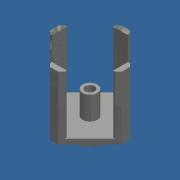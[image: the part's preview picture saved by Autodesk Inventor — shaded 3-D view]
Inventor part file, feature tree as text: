
AUTODESK INVENTOR PART (.ipt)
format: ipt  version: 2020 (Build 240168000, 168)  size: 2,207,232 bytes
history: mixed  units: mm
features: sketch x5, extrude x4, hole x1, pattern_circular x1, chamfer x1, fillet x1, imported_body x1
ambient origin geometry x8: Origin, YZ Plane, XZ Plane, XY Plane, X Axis, Y Axis, Z Axis, Center Point
bodies: Solid1 (imported_parasolid)
feature tree (14):
  extrude  "Extrusion1"  Depth=4.0mm TaperAngle=0.0deg
  extrude  "Extrusion3"  Depth=68.0mm
  extrude  "Extrusion4"  Depth=14.0mm
  extrude  "Extrusion5"  Depth=5.0mm
  hole  "Hole6"  [1 undecoded]
  pattern_circular  "Circular Pattern2"  [2 undecoded]
  chamfer  "Chamfer2"  Distance=14.0mm
  sketch  "Sketch1"  dims[d0=35.0mm d1=4.0mm d2=0.0mm]
  sketch  "Sketch4"  dims[d42=68.0mm d43=68.0mm]
  sketch  "Sketch5"  dims[d44=5.0mm d45=0.0mm d46=14.0mm]
  sketch  "Sketch7"  dims[d47=5.0mm d48=29.0mm]
  sketch  "Sketch8"  dims[d49=7.0mm d50=55.0mm d51=0.0mm d69=4.0mm d70=0.0mm d78=14.0mm d79=22.0mm d80=0.0mm d81=8.5mm d82=6.0mm d83=4.0mm d84=2.0mm d85=90.0deg d86=51.6mm d87=0.0mm d88=40.0mm d89=360.0deg d91=30.0mm d92=2.0mm d93=45.0deg]
  fillet  "Redondeo2"  Radius=22.0mm
  imported_body  NMx_Import_Brep_tag  [imported B-rep: ~996 faces, bbox_mm=[68.0, 68.0, 68.0]]
note: 3 required parameter values undecoded (feature->parameter linkage not recoverable at this tier; creation-order binding heuristic only, values carry confidence <= 0.55)
